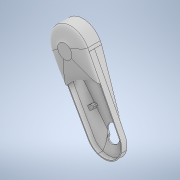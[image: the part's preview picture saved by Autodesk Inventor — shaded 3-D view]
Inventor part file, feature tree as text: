
AUTODESK INVENTOR PART (.ipt)
format: ipt  version: 2020.1 (Build 241239000, 239)  size: 2,710,528 bytes
history: native  units: mm
features: other x17, sketch x11, extrude x6, surface_op x6, plane x3, loft x2, reference x2, shell x1, hole x1, chamfer x1, projected_geometry x1
ambient origin geometry x8: Origin, YZ Plane, XZ Plane, XY Plane, X Axis, Y Axis, Z Axis, Center Point
bodies: Body1 (feature_tree), Body2 (feature_tree), Body3 (feature_tree), Body4 (feature_tree), Body5 (feature_tree), Body6 (feature_tree), Body7 (feature_tree), Body8 (feature_tree)
feature tree (51):
  other  "Lenkerhuelle"
  other  "Chain"
  plane  "Work Plane1"
  sketch  "Sketch2"  dims[d0=75.0mm d1=95.0mm]
  plane  "Work Plane2"
  loft  "Loft1"
  extrude  "Extrusion1"  Depth=5.0mm
  shell  "Shell1"  Thickness=11.0mm
  extrude  "Extrusion2"  Depth=1.0mm
  extrude  "Extrusion3"  Depth=10.0mm TaperAngle=0.0deg
  sketch  "Sketch8"  dims[d19=97.0mm d21=3.0mm]
  hole  "Hole1"  [1 undecoded]
  plane  "Work Plane3"
  loft  "Loft2"
  extrude  "Extrusion5"  Depth=0.2mm
  extrude  "Extrusion6"  TaperAngle=0.0deg  [1 undecoded]
  extrude  "Extrusion7"  Depth=10.0mm TaperAngle=0.0deg
  chamfer  "Chamfer1"  Distance=5.0mm
  reference  "Reference1"
  reference  "Reference2"
  sketch  "Sketch3"  dims[d3=2.0mm d4=5.0mm]
  sketch  "Sketch5"  dims[d5=0.0mm d6=90.0deg d7=0.0mm d8=90.0deg d11=11.0mm d12=0.0mm]
  projected_geometry  "Projected Loop1"
  sketch  "Sketch6"  dims[d13=2.0mm d14=1.0mm]
  sketch  "Sketch7"  dims[d15=0.0mm d16=0.0mm d17=10.0mm d18=0.0mm]
  sketch  "Sketch9"  dims[d22=3.0mm d23=10.0mm d24=90.0deg]
  sketch  "Sketch10"  dims[d28=0.2mm d31=0.2mm]
  sketch  "Sketch11"  dims[d32=10.0mm d33=0.0mm d34=0.0mm d35=90.0deg]
  other  "Lenkerabdeckung"
  sketch  "Sketch12"  dims[d36=8.2mm d37=10.0mm d38=0.0mm]
  sketch  "Sketch13"  dims[d39=8.2mm d40=5.0mm d41=0.0mm d42=5.0mm d43=5.98424mm d44=4.0mm d45=2.0mm d46=90.0deg d47=10.688mm d48=0.0mm d49=2.0mm d50=2.0mm d51=45.0deg d20=0.872665mm]
  surface_op  "Surface1"
  surface_op  "Surface2"
  surface_op  "Surface3"
  surface_op  "Surface4"
  surface_op  "Surface5"
  surface_op  "Surface6"
  other  "<userpath>\Desktop\URBANT ROVER\rover.iam"
  other  "rover.iam"
  other  "axle R"
  other  "rear axle"
  other  "Srf1"
  other  "Srf2"
  other  "Srf3"
  other  "Srf4"
  other  "Srf5"
  other  "Srf6"
  other  "Rad mit Aufnahme.6"
  other  "Kettenradaufnahme.1"
  other  "drive shaft.1"
  other  "Axle Nut.1"
note: 2 required parameter values undecoded (feature->parameter linkage not recoverable at this tier; creation-order binding heuristic only, values carry confidence <= 0.55)
